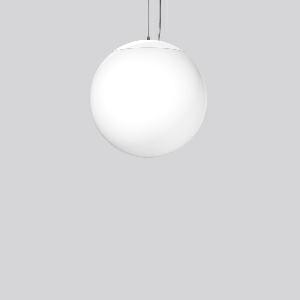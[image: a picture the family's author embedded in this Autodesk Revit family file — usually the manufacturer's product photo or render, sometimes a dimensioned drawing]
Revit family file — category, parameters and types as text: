
# Revit family: basic_ball_312109_002_4344
name_source: partatom
category: Lighting Fixtures
units: mm (PartAtom-declared; Revit-internal decimal feet)

## family parameters
Cut with Voids When Loaded = No
Host = Face
Light Source = No
Part Type = Normal
Room Calculation Point = No
Round Connector Dimension = Use Diameter
Shared = No

## types (1)
- BASIC BALL (1 x LED Modul 830, 2550 lm, 3000)
    Apparent Load = 28 VA
    Approval mark = CE
    CIE Flux Codes = 25 51 76 59 100
    Color Rendering = 80
    Color Temperature = 3000
    Default Elevation = 1800 mm
    Description = Series: BASIC BALL
Pendant luminaire in timelessly classic sphere design. Canopy: metal, powder-coated, white. Metal cap: white, powder-coated. Diffuser: shockproof plastic (polyethylene), opal, satin finish. Shadow-free, homogeneous and soft illumination
    Height = 350 mm
    Lamp = 1 x LED Modul 830
    Lamp Light Flux = 2550 lm
    Lamp count = 1
    Length = 350 mm
    Lifetime = 50000 h
    Luminous efficacy = 91 lm/W
    Manufacturer = RZB
    ModVariant = No
    Model = 312109.002
    Mounting Place = Ceiling
    Mounting Type = Pendant
    Number of Poles = 1
    OnlyDefault = Yes
    Power Factor = 1
    Product Name = BASIC BALL
    Product group = Pendant luminaires
    ProductGroupID = 902
    Protection Class = Protection class I
    Protection Degree = IP 40
    RLX_Detail_Level = 1
    RLX_Emergency_Light_Flux = 0 lm
    RLX_Emergency_Type = 0
    RLX_Emergency_Type_DB = No
    RlxData = <blob elided: 52517 chars, md5=cb8ac2f8>
    Socket = socket
    Standby Power = 0 W
    System Light Flux = 2550 lm
    System Power = 28 W
    Type Comments = Product without accessories
    Type Image = 312105.002.jpg
    URL = http://relux.com
    VarID = ---
    Voltage = 230 V
    Voltage Range = 220-240 V
    Weight = 0.00 kg
    Width = 0 mm  [stored 0 ft]

note: [stored X ft] marks values corroborated as IEEE doubles in the binary element streams (Revit-internal decimal feet)

## geometry (parser evidence)
native form markers: Blend x4, Sweep x14
no freeform markers — native parametric forms only
